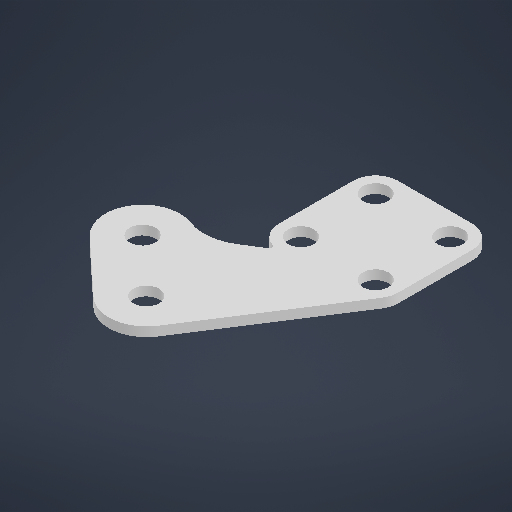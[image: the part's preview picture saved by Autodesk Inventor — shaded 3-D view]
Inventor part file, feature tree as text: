
AUTODESK INVENTOR PART (.ipt)
format: ipt  version: 2025.2 (Build 292293000, 293)  size: 228,352 bytes
history: native  units: in
note: dims shown in document units (in); Inventor stores cm internally (conversion verified against a paired STEP export)
features: extrude x1, sketch x1
ambient origin geometry x8: Origin, YZ Plane, XZ Plane, XY Plane, X Axis, Y Axis, Z Axis, Center Point
bodies: Solid1 (feature_tree)
feature tree (2):
  extrude  "Extrusion1"  [1 undecoded]
  sketch  "Sketch1"  dims[d8=0.0625in d9=0.0in]
note: 1 required parameter value undecoded (feature->parameter linkage not recoverable at this tier; creation-order binding heuristic only, values carry confidence <= 0.55)
